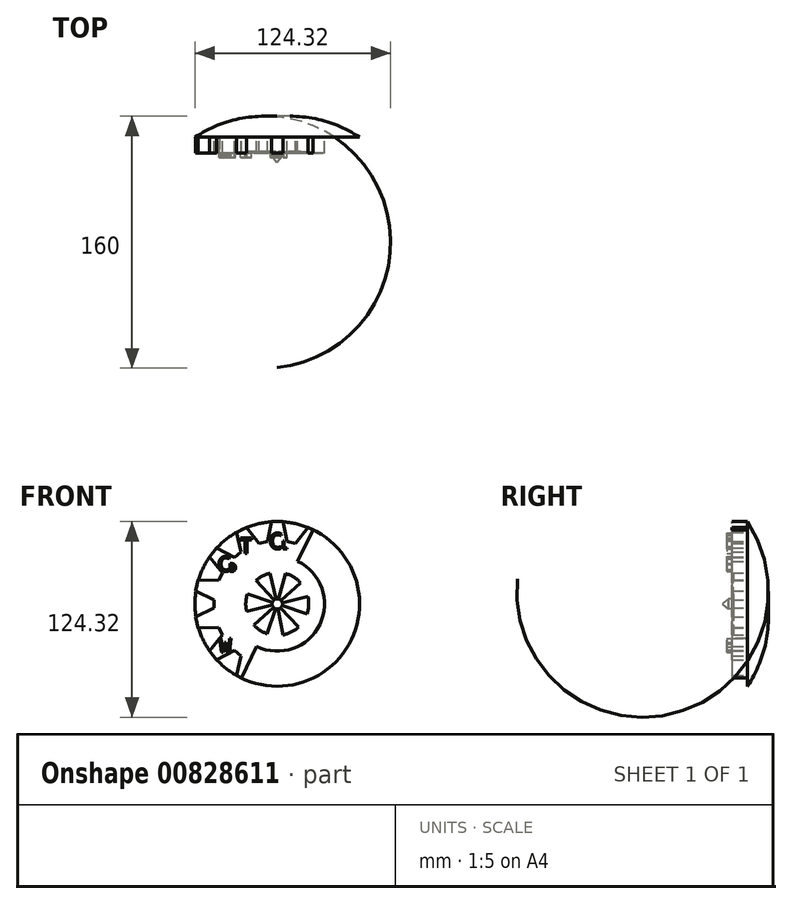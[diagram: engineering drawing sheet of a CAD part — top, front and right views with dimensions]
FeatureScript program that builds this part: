
annotation { "Feature Type Name" : "Feature", "Feature Type Description" : "" }
export const myFeature = defineFeature(function(context is Context, id is Id, definition is map)
    precondition{}
    {
        {
            var Q0;
            Q0=qCreatedBy(makeId("Front.planeOp"),FACE);
            var sketch = newSketch(context, id + "F0", { "sketchPlane" : qUnion([Q0])});
            skCircle(sketch, "E0", {"center": v(0, 0) * mm, "radius": 20 * mm});
            skCircle(sketch, "E1", {"center": v(0, 0) * mm, "radius": 30 * mm});
            skArc(sketch, "E2", {"start": v(17.36, 36.04) * mm, "mid": v(-36.04, 17.36) * mm, "end": v(-17.36, -36.04) * mm});
            skArc(sketch, "E3.cCircle", {"start": v(17.36, 36.04) * mm, "mid": v(-36.04, 17.36) * mm, "end": v(-17.36, -36.04) * mm, "construction": true});
            skLineSegment(sketch, "E3.7", {"start": v(-17.8, -36.97) * mm, "end": v(-32.08, -25.58) * mm});
            skLineSegment(sketch, "E3.8", {"start": v(-32.08, -25.58) * mm, "end": v(-40, -9.13) * mm});
            skLineSegment(sketch, "E3.9", {"start": v(-40, -9.13) * mm, "end": v(-40, 9.13) * mm});
            skLineSegment(sketch, "E3.10", {"start": v(-40, 9.13) * mm, "end": v(-32.08, 25.58) * mm});
            skLineSegment(sketch, "E3.11", {"start": v(-32.08, 25.58) * mm, "end": v(-17.8, 36.97) * mm});
            skLineSegment(sketch, "E3.12", {"start": v(-17.8, 36.97) * mm, "end": v(0, 41.03) * mm});
            skLineSegment(sketch, "E3.13", {"start": v(0, 41.03) * mm, "end": v(17.8, 36.97) * mm});
            skPoint(sketch, "E4", {"position": v(0, 54.03) * mm});
            skPoint(sketch, "E5", {"position": v(-8.9, 39) * mm});
            skLineSegment(sketch, "E6", {"start": v(-3.6, 52.3) * mm, "end": v(-6.34, 39.58) * mm});
            skLineSegment(sketch, "E7", {"start": v(6.34, 39.58) * mm, "end": v(3.6, 52.3) * mm});
            skLineSegment(sketch, "E8", {"start": v(-3.6, 52.3) * mm, "end": v(3.6, 52.3) * mm});
            skLineSegment(sketch, "E9", {"start": v(11.46, 38.41) * mm, "end": v(19.44, 48.68) * mm});
            skLineSegment(sketch, "E10", {"start": v(19.44, 48.68) * mm, "end": v(22.69, 47.11) * mm});
            skLineSegment(sketch, "E11", {"start": v(-11.46, 38.41) * mm, "end": v(-19.44, 48.68) * mm});
            skLineSegment(sketch, "E12", {"start": v(-19.44, 48.68) * mm, "end": v(-25.93, 45.55) * mm});
            skLineSegment(sketch, "E13", {"start": v(-25.93, 45.55) * mm, "end": v(-22.88, 32.91) * mm});
            skLineSegment(sketch, "E14", {"start": v(-27, 29.63) * mm, "end": v(-38.64, 35.42) * mm});
            skLineSegment(sketch, "E15", {"start": v(-38.64, 35.42) * mm, "end": v(-43.13, 29.79) * mm});
            skLineSegment(sketch, "E16", {"start": v(-43.13, 29.79) * mm, "end": v(-34.9, 19.72) * mm});
            skLineSegment(sketch, "E17", {"start": v(-37.18, 14.99) * mm, "end": v(-50.18, 15.15) * mm});
            skLineSegment(sketch, "E18", {"start": v(-50.18, 15.15) * mm, "end": v(-51.78, 8.12) * mm});
            skLineSegment(sketch, "E19", {"start": v(-51.78, 8.12) * mm, "end": v(-40, 2.63) * mm});
            skLineSegment(sketch, "E20", {"start": v(-51.78, -8.12) * mm, "end": v(-50.18, -15.15) * mm});
            skLineSegment(sketch, "E21", {"start": v(-34.9, -19.72) * mm, "end": v(-43.13, -29.79) * mm});
            skLineSegment(sketch, "E22", {"start": v(-22.88, -32.91) * mm, "end": v(-25.93, -45.55) * mm});
            skLineSegment(sketch, "E23", {"start": v(-51.78, -8.12) * mm, "end": v(-40, -2.63) * mm});
            skLineSegment(sketch, "E24", {"start": v(-50.18, -15.15) * mm, "end": v(-37.18, -14.99) * mm});
            skLineSegment(sketch, "E25", {"start": v(-38.64, -35.42) * mm, "end": v(-27, -29.63) * mm});
            skLineSegment(sketch, "E26", {"start": v(-43.13, -29.79) * mm, "end": v(-38.64, -35.42) * mm});
            skLineSegment(sketch, "E27", {"start": v(-25.93, -45.55) * mm, "end": v(-22.69, -47.11) * mm});
            skPoint(sketch, "E28", {"position": v(22.69, 47.11) * mm});
            skPoint(sketch, "E29", {"position": v(-22.69, -47.11) * mm});
            skLineSegment(sketch, "E30", {"start": v(22.69, 47.11) * mm, "end": v(-22.69, -47.11) * mm});
            skPoint(sketch, "E31.orphan", {"position": v(0, -41.03) * mm});
            skPoint(sketch, "E32.orphan", {"position": v(-19.44, -48.68) * mm});
            skPoint(sketch, "E33.orphan", {"position": v(17.8, -36.97) * mm});
            skPoint(sketch, "E34.orphan", {"position": v(40, -9.13) * mm});
            skPoint(sketch, "E35.orphan", {"position": v(25.93, 45.55) * mm});
            skSolve(sketch);
        }
        {
            var Q0;
            Q0=qCreatedBy(makeId("Top.planeOp"),FACE);
            var sketch = newSketch(context, id + "F1", { "sketchPlane" : qUnion([Q0])});
            skLineSegment(sketch, "E36", {"start": v(-52.3, 0) * mm, "end": v(0, 0) * mm});
            skLineSegment(sketch, "E37", {"start": v(0, 0) * mm, "end": v(0, 13) * mm});
            skArc(sketch, "E38", {"start": v(0, 13) * mm, "mid": v(-27.28, 11.04) * mm, "end": v(-52.3, 0) * mm});
            skSolve(sketch);
        }
        {
            var Q0;
            Q0=makeQuery(id+"F0.imprint","IMPRINT",FACE,{"disambiguationData":[TD([[makeQuery(id+"F0.imprint","IMPRINT",EDGE,{"derivedFrom":sQuery(id+"F0.wireOp",EDGE,"E1")}),-1.0]])]});
            var Q1;
            Q1=makeQuery(id+"F0.imprint","IMPRINT",FACE,{"disambiguationData":[TD([[makeQuery(id+"F0.imprint","IMPRINT",EDGE,{"derivedFrom":sQuery(id+"F0.wireOp",EDGE,"E0")}),-1.0]])]});
            var Q2;
            Q2=makeQuery(id+"F0.imprint","IMPRINT",FACE,{"disambiguationData":[TD([[makeQuery(id+"F0.imprint","IMPRINT",EDGE,{"derivedFrom":sQuery(id+"F0.wireOp",EDGE,"E0")}),1.0]])]});
            var Q3;
            {var subQ3=sQuery(id+"F0.wireOp",EDGE,"E14");Q3=makeQuery(id+"F0.imprint","IMPRINT",FACE,{"disambiguationData":[TD([[makeQuery(id+"F0.imprint","IMPRINT",EDGE,{"derivedFrom":subQ3}),1.0]])]});}
            var Q4;
            {var subQ3=sQuery(id+"F0.wireOp",EDGE,"E11");Q4=makeQuery(id+"F0.imprint","IMPRINT",FACE,{"disambiguationData":[TD([[makeQuery(id+"F0.imprint","IMPRINT",EDGE,{"derivedFrom":subQ3}),1.0]])]});}
            var Q5;
            Q5 = qSketchRegion(id + "F0", true);
            extrude(context, id + "F2", {"entities" : qUnion([Q0, Q1, Q2, Q3, Q4, Q5]), "depth" : 10 * mm, "offsetDistance" : 25 * mm});
        }
        {
            var Q0;
            Q0=makeQuery(id+"F1.imprint","IMPRINT",FACE,{"disambiguationData":[TD([[makeQuery(id+"F1.imprint","IMPRINT",EDGE,{"derivedFrom":sQuery(id+"F1.wireOp",EDGE,"E36")}),1.0]])]});
            var Q1;
            Q1=sQuery(id+"F0.wireOp",EDGE,"E0");
            revolve(context, id + "F3", {"operationType" : NewBodyOperationType.ADD, "surfaceOperationType" : NewSurfaceOperationType.NEW, "entities" : qUnion([Q0]), "axis" : qUnion([Q1]), "revolveType" : RevolveType.FULL});
        }
        {
            var Q0;
            {var subQ5=sQuery(id+"F0.wireOp",EDGE,"E1");Q0=makeQuery(id+"F3.boolean.opBoolean","SPLIT",FACE,{"disambiguationData":[TD([makeQuery(id+"F2.opExtrude","SWEPT_FACE",FACE,{"disambiguationData":[OSD([subQ5])]})])],"derivedFrom":makeQuery(id+"F3.opRevolve","SWEPT_FACE",FACE,{"disambiguationData":[OSD([sQuery(id+"F1.wireOp",EDGE,"E36")])]})});}
            var sketch = newSketch(context, id + "F4", { "sketchPlane" : qUnion([Q0])});
            skText(sketch, "E39", { "text": "T", "fontName": "DroidSansMono.ttf"});
            skLineSegment(sketch, "E40.0", {"start": v(-11.46, 38.41) * mm, "end": v(-19.44, 48.68) * mm});
            skText(sketch, "E41", { "text": "C", "fontName": "DroidSansMono.ttf"});
            skLineSegment(sketch, "E42.0", {"start": v(-3.6, 52.3) * mm, "end": v(-6.34, 39.58) * mm});
            skText(sketch, "E43", { "text": "L", "fontName": "DroidSansMono.ttf"});
            skText(sketch, "E44", { "text": "C", "fontName": "DroidSansMono.ttf"});
            skText(sketch, "E45", { "text": "D", "fontName": "DroidSansMono.ttf"});
            skLineSegment(sketch, "E46.0", {"start": v(-27, 29.63) * mm, "end": v(-38.64, 35.42) * mm});
            skText(sketch, "E47", { "text": "W", "fontName": "DroidSansMono.ttf"});
            skLineSegment(sketch, "E48.0", {"start": v(-34.9, -19.72) * mm, "end": v(-43.13, -29.79) * mm});
            const initialGuessF4  = {"E39": [-0.02394, 0.03197, 1, 0, 0.01], "E41": [-0.00517, 0.035, 1, 0, 0.01], "E43": [0.00274, 0.035, 1, 0, 0.005], "E44": [-0.03778, 0.02073, 1, 0, 0.0095], "E45": [-0.03036, 0.02062, 1, 0, 0.005], "E47": [-0.03677, -0.03076, 1, 0, 0.009]};
            skSetInitialGuess(sketch, initialGuessF4);
            skSolve(sketch);
        }
        {
            var Q0;
            Q0 = qSketchRegion(id + "F4", true);
            extrude(context, id + "F5", {"entities" : qUnion([Q0]), "operationType" : NewBodyOperationType.ADD, "depth" : 13 * mm, "offsetDistance" : 25 * mm});
        }
        {
            var Q0;
            {var subQ0=sQuery(id+"F0.wireOp",EDGE,"E18");var subQ1=sQuery(id+"F0.wireOp",EDGE,"E17");var subQ2=sQuery(id+"F0.wireOp",EDGE,"E16");var subQ3=sQuery(id+"F0.wireOp",EDGE,"E15");var subQ4=sQuery(id+"F0.wireOp",EDGE,"E14");var subQ5=sQuery(id+"F0.wireOp",EDGE,"E13");var subQ6=sQuery(id+"F0.wireOp",EDGE,"E12");var subQ7=sQuery(id+"F0.wireOp",EDGE,"E11");var subQ8=sQuery(id+"F0.wireOp",EDGE,"E10");var subQ9=sQuery(id+"F0.wireOp",EDGE,"E9");var subQ10=sQuery(id+"F0.wireOp",EDGE,"E8");var subQ11=sQuery(id+"F0.wireOp",EDGE,"E3.8");var subQ12=sQuery(id+"F0.wireOp",EDGE,"E3.7");var subQ13=sQuery(id+"F0.wireOp",EDGE,"E3.9");var subQ14=sQuery(id+"F0.wireOp",EDGE,"E19");var subQ15=sQuery(id+"F0.wireOp",EDGE,"E1");var subQ16=sQuery(id+"F0.wireOp",EDGE,"E7");var subQ17=sQuery(id+"F0.wireOp",EDGE,"E3.10");var subQ18=sQuery(id+"F0.wireOp",EDGE,"E3.11");var subQ19=sQuery(id+"F0.wireOp",EDGE,"E3.12");var subQ20=sQuery(id+"F0.wireOp",EDGE,"E3.13");var subQ21=sQuery(id+"F0.wireOp",EDGE,"E6");var subQ22=sQuery(id+"F0.wireOp",EDGE,"E20");var subQ23=sQuery(id+"F0.wireOp",EDGE,"E21");var subQ24=sQuery(id+"F0.wireOp",EDGE,"E22");var subQ25=sQuery(id+"F0.wireOp",EDGE,"E23");var subQ26=sQuery(id+"F0.wireOp",EDGE,"E24");var subQ27=sQuery(id+"F0.wireOp",EDGE,"E25");var subQ28=sQuery(id+"F0.wireOp",EDGE,"E27");var subQ29=sQuery(id+"F0.wireOp",EDGE,"E26");var subQ30=sQuery(id+"F0.wireOp",EDGE,"E30");Q0=makeQuery(id+"F5.boolean.opBoolean","SPLIT",FACE,{"disambiguationData":[TD([makeQuery(id+"F2.opExtrude","SWEPT_FACE",FACE,{"disambiguationData":[OSD([subQ15])]})])],"derivedFrom":makeQuery(id+"F2.opExtrude","CAP_FACE",FACE,{"disambiguationData":[OSD([subQ15,subQ12,subQ11,subQ13,subQ17,subQ18,subQ19,subQ20,subQ21,subQ16,subQ10,subQ9,subQ8,subQ7,subQ6,subQ5,subQ4,subQ3,subQ2,subQ1,subQ0,subQ14,subQ22,subQ23,subQ24,subQ25,subQ26,subQ27,subQ29,subQ28,subQ30])],"isStart":false})});}
            var sketch = newSketch(context, id + "F6", { "sketchPlane" : qUnion([Q0])});
            skCircle(sketch, "E49", {"center": v(0, 0) * mm, "radius": 20 * mm});
            skLineSegment(sketch, "E50", {"start": v(0.87, 3.13) * mm, "end": v(5.34, 19.27) * mm});
            skLineSegment(sketch, "E51", {"start": v(2.4, 2.2) * mm, "end": v(14.77, 13.5) * mm});
            skLineSegment(sketch, "E52", {"start": v(-0.76, 3.16) * mm, "end": v(-4.66, 19.45) * mm});
            skLineSegment(sketch, "E53", {"start": v(-2.2, 2.4) * mm, "end": v(-13.5, 14.77) * mm});
            skLineSegment(sketch, "E54", {"start": v(-3.08, 1.04) * mm, "end": v(-18.95, 6.39) * mm});
            skLineSegment(sketch, "E55", {"start": v(-3.16, -0.76) * mm, "end": v(-19.45, -4.66) * mm});
            skLineSegment(sketch, "E56", {"start": v(-2.4, -2.2) * mm, "end": v(-14.77, -13.5) * mm});
            skLineSegment(sketch, "E57", {"start": v(-1.04, -3.08) * mm, "end": v(-6.39, -18.95) * mm});
            skLineSegment(sketch, "E58", {"start": v(0.58, -3.2) * mm, "end": v(3.58, -19.68) * mm});
            skLineSegment(sketch, "E59", {"start": v(2.2, -2.4) * mm, "end": v(13.5, -14.77) * mm});
            skLineSegment(sketch, "E60", {"start": v(3.08, -1.04) * mm, "end": v(18.95, -6.39) * mm});
            skLineSegment(sketch, "E61", {"start": v(3.16, 0.76) * mm, "end": v(19.45, 4.66) * mm});
            skCircle(sketch, "E62", {"center": v(0, 0) * mm, "radius": 3.25 * mm});
            skSolve(sketch);
        }
        {
            var Q0;
            {var subQ0=sQuery(id+"F6.wireOp",EDGE,"E52");var subQ1=sQuery(id+"F6.wireOp",EDGE,"E49");var subQ2=makeQuery(id+"F6.imprint","INTERSECT",VERTEX,{"derivedFrom":[subQ1,subQ0]});Q0=makeQuery(id+"F6.imprint","IMPRINT",FACE,{"disambiguationData":[TD([[makeQuery(id+"F6.imprint","IMPRINT",EDGE,{"disambiguationData":[TD([[subQ2,-1.0]])],"derivedFrom":subQ1}),1.0]])]});}
            var Q1;
            {var subQ0=sQuery(id+"F6.wireOp",EDGE,"E50");var subQ1=sQuery(id+"F6.wireOp",EDGE,"E49");var subQ2=makeQuery(id+"F6.imprint","INTERSECT",VERTEX,{"derivedFrom":[subQ1,subQ0]});Q1=makeQuery(id+"F6.imprint","IMPRINT",FACE,{"disambiguationData":[TD([[makeQuery(id+"F6.imprint","IMPRINT",EDGE,{"disambiguationData":[TD([[subQ2,1.0]])],"derivedFrom":subQ1}),1.0]])]});}
            var Q2;
            {var subQ0=sQuery(id+"F6.wireOp",EDGE,"E60");var subQ1=sQuery(id+"F6.wireOp",EDGE,"E49");var subQ2=makeQuery(id+"F6.imprint","INTERSECT",VERTEX,{"derivedFrom":[subQ1,subQ0]});Q2=makeQuery(id+"F6.imprint","IMPRINT",FACE,{"disambiguationData":[TD([[makeQuery(id+"F6.imprint","IMPRINT",EDGE,{"disambiguationData":[TD([[subQ2,-1.0]])],"derivedFrom":subQ1}),1.0]])]});}
            var Q3;
            {var subQ0=sQuery(id+"F6.wireOp",EDGE,"E58");var subQ1=sQuery(id+"F6.wireOp",EDGE,"E49");var subQ2=makeQuery(id+"F6.imprint","INTERSECT",VERTEX,{"derivedFrom":[subQ1,subQ0]});Q3=makeQuery(id+"F6.imprint","IMPRINT",FACE,{"disambiguationData":[TD([[makeQuery(id+"F6.imprint","IMPRINT",EDGE,{"disambiguationData":[TD([[subQ2,-1.0]])],"derivedFrom":subQ1}),1.0]])]});}
            var Q4;
            {var subQ0=sQuery(id+"F6.wireOp",EDGE,"E56");var subQ1=sQuery(id+"F6.wireOp",EDGE,"E49");var subQ2=makeQuery(id+"F6.imprint","INTERSECT",VERTEX,{"derivedFrom":[subQ1,subQ0]});Q4=makeQuery(id+"F6.imprint","IMPRINT",FACE,{"disambiguationData":[TD([[makeQuery(id+"F6.imprint","IMPRINT",EDGE,{"disambiguationData":[TD([[subQ2,-1.0]])],"derivedFrom":subQ1}),1.0]])]});}
            var Q5;
            {var subQ0=sQuery(id+"F6.wireOp",EDGE,"E54");var subQ1=sQuery(id+"F6.wireOp",EDGE,"E49");var subQ2=makeQuery(id+"F6.imprint","INTERSECT",VERTEX,{"derivedFrom":[subQ1,subQ0]});Q5=makeQuery(id+"F6.imprint","IMPRINT",FACE,{"disambiguationData":[TD([[makeQuery(id+"F6.imprint","IMPRINT",EDGE,{"disambiguationData":[TD([[subQ2,-1.0]])],"derivedFrom":subQ1}),1.0]])]});}
            extrude(context, id + "F7", {"entities" : qUnion([Q0, Q1, Q2, Q3, Q4, Q5]), "operationType" : NewBodyOperationType.REMOVE, "oppositeDirection" : true, "depth" : 1 * mm, "offsetDistance" : 25 * mm});
        }
        {
            var Q0;
            Q0=qCreatedBy(makeId("Top.planeOp"),FACE);
            var sketch = newSketch(context, id + "F8", { "sketchPlane" : qUnion([Q0])});
            skPoint(sketch, "E63.0", {"position": v(0, -10) * mm});
            skLineSegment(sketch, "E64", {"start": v(0, -10) * mm, "end": v(3.25, -10) * mm});
            skLineSegment(sketch, "E65", {"start": v(0, -16) * mm, "end": v(0, -10) * mm});
            skLineSegment(sketch, "E66", {"start": v(3.25, -10) * mm, "end": v(3.25, -12) * mm});
            skLineSegment(sketch, "E67", {"start": v(3.25, -12) * mm, "end": v(0, -16) * mm});
            skSolve(sketch);
        }
        {
            var Q0;
            Q0=makeQuery(id+"F8.imprint","IMPRINT",FACE,{"disambiguationData":[TD([[makeQuery(id+"F8.imprint","IMPRINT",EDGE,{"derivedFrom":sQuery(id+"F8.wireOp",EDGE,"E64")}),-1.0]])]});
            var Q1;
            Q1=sQuery(id+"F6.wireOp",EDGE,"E62");
            revolve(context, id + "F9", {"operationType" : NewBodyOperationType.ADD, "surfaceOperationType" : NewSurfaceOperationType.NEW, "entities" : qUnion([Q0]), "axis" : qUnion([Q1]), "revolveType" : RevolveType.FULL});
        }
        {
            var Q0;
            {var subQ0=sQuery(id+"F6.wireOp",EDGE,"E62");var subQ8=makeQuery(id+"F6.imprint","INTERSECT",VERTEX,{"derivedFrom":[sQuery(id+"F6.wireOp",EDGE,"E51"),subQ0]});Q0=makeQuery(id+"F6.imprint","IMPRINT",FACE,{"disambiguationData":[TD([[makeQuery(id+"F6.imprint","IMPRINT",EDGE,{"disambiguationData":[TD([[subQ8,1.0]])],"derivedFrom":subQ0}),1.0]])]});}
            extrude(context, id + "F10", {"entities" : qUnion([Q0]), "operationType" : NewBodyOperationType.ADD, "depth" : 2 * mm, "offsetDistance" : 25 * mm});
        }
    });
